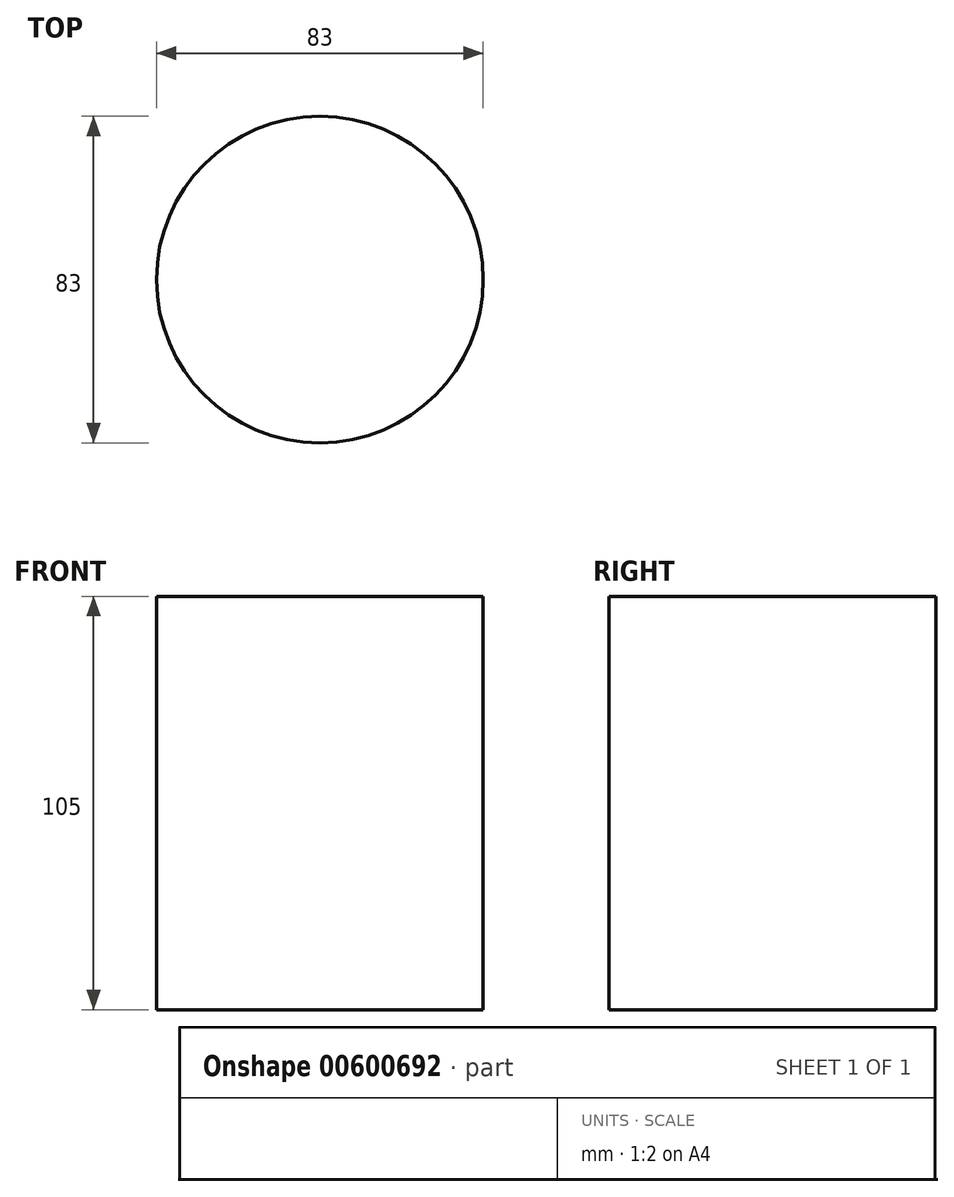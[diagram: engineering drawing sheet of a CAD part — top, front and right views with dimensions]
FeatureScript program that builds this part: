
annotation { "Feature Type Name" : "Feature", "Feature Type Description" : "" }
export const myFeature = defineFeature(function(context is Context, id is Id, definition is map)
    precondition{}
    {
        {
            var Q0;
            Q0=qCreatedBy(makeId("Top.planeOp"),FACE);
            var sketch = newSketch(context, id + "F0", { "sketchPlane" : qUnion([Q0])});
            skCircle(sketch, "E0", {"center": v(0, 0) * mm, "radius": 41.5 * mm});
            skSolve(sketch);
        }
        {
            var Q0;
            Q0=makeQuery(id+"F0.imprint","IMPRINT",FACE,{"disambiguationData":[TD([[makeQuery(id+"F0.imprint","IMPRINT",EDGE,{"derivedFrom":sQuery(id+"F0.wireOp",EDGE,"E0")}),1.0]])]});
            extrude(context, id + "F1", {"entities" : qUnion([Q0]), "depth" : 105 * mm, "offsetDistance" : 25 * mm});
        }
        {
            var Q0;
            Q0=qCreatedBy(makeId("Right.planeOp"),FACE);
            cPlane(context, id + "F2", {"entities" : qUnion([Q0]), "cplaneType" : CPlaneType.OFFSET, "offset" : 41 * mm, "width" : 150 * mm, "height" : 150 * mm});
        }
    });
